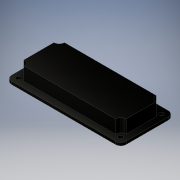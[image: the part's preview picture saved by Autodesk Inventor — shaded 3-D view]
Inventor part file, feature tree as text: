
AUTODESK INVENTOR PART (.ipt)
format: ipt  version: 2019 (Build 230136000, 136)  size: 154,624 bytes
history: native  units: mm
features: extrude x2, sketch x2
ambient origin geometry x8: Origin, YZ Plane, XZ Plane, XY Plane, X Axis, Y Axis, Z Axis, Center Point
bodies: Solid1 (feature_tree)
feature tree (4):
  extrude  "Extrusion1"  Depth=30.0mm
  extrude  "Extrusion3"  Depth=7.5mm
  sketch  "Sketch1"  dims[d0=65.0mm d1=30.0mm]
  sketch  "Sketch2"  dims[d2=3.0mm d3=2.5mm d4=3.5mm d5=3.5mm d6=20.0mm d8=23.0mm d9=20.0mm d11=58.0mm d14=1.6mm d15=0.0mm d17=6.0mm d18=20.0mm d20=23.0mm d21=20.0mm d23=58.0mm d28=7.0mm d29=7.0mm d30=7.5mm d31=0.0mm]
